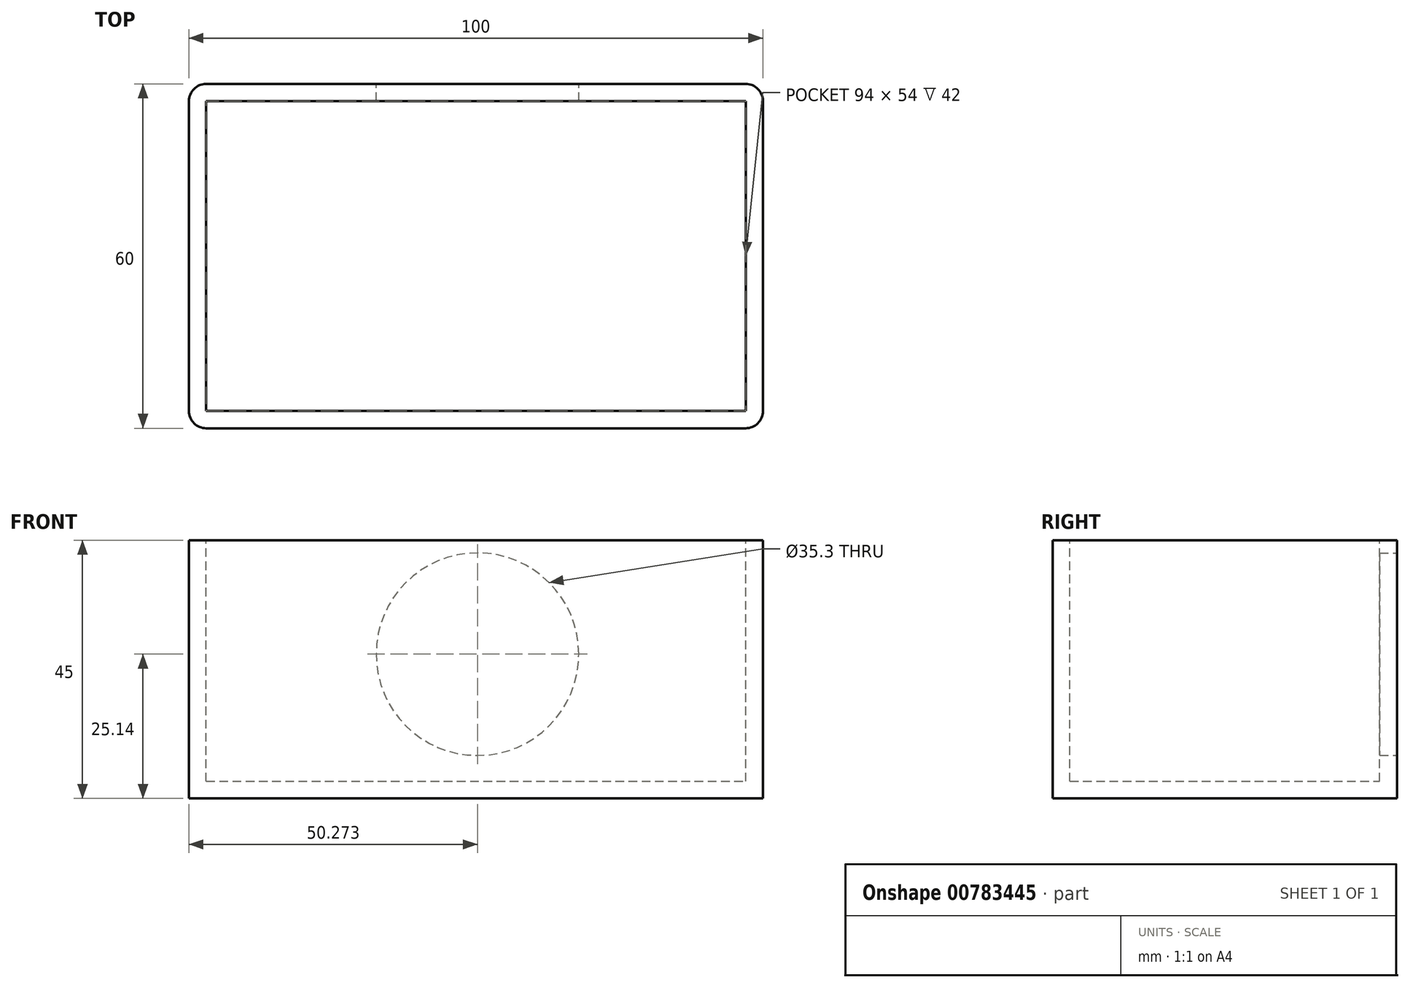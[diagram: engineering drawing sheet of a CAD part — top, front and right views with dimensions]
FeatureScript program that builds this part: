
annotation { "Feature Type Name" : "Feature", "Feature Type Description" : "" }
export const myFeature = defineFeature(function(context is Context, id is Id, definition is map)
    precondition{}
    {
        {
            var Q0;
            Q0=qCreatedBy(makeId("Top.planeOp"),FACE);
            var sketch = newSketch(context, id + "F0", { "sketchPlane" : qUnion([Q0])});
            skLineSegment(sketch, "E0", {"start": v(100, 0) * mm, "end": v(0, 0) * mm});
            skLineSegment(sketch, "E1", {"start": v(0, 0) * mm, "end": v(0, -60) * mm});
            skLineSegment(sketch, "E2", {"start": v(0, -60) * mm, "end": v(100, -60) * mm});
            skLineSegment(sketch, "E3", {"start": v(100, -60) * mm, "end": v(100, 0) * mm});
            skSolve(sketch);
        }
        {
            var Q0;
            Q0 = qSketchRegion(id + "F0", true);
            extrude(context, id + "F1", {"entities" : qUnion([Q0]), "depth" : 45 * mm, "offsetDistance" : 25 * mm});
        }
        {
            var Q0;
            Q0=makeQuery(id+"F1.opExtrude","CAP_FACE",FACE,{"disambiguationData":[OSD([sQuery(id+"F0.wireOp",EDGE,"E0"),sQuery(id+"F0.wireOp",EDGE,"E1"),sQuery(id+"F0.wireOp",EDGE,"E2"),sQuery(id+"F0.wireOp",EDGE,"E3")])],"isStart":false});
            var sketch = newSketch(context, id + "F2", { "sketchPlane" : qUnion([Q0])});
            skLineSegment(sketch, "E4.bottom", {"start": v(97, -3) * mm, "end": v(3, -3) * mm});
            skLineSegment(sketch, "E4.top", {"start": v(97, -57) * mm, "end": v(3, -57) * mm});
            skLineSegment(sketch, "E4.left", {"start": v(97, -3) * mm, "end": v(97, -57) * mm});
            skLineSegment(sketch, "E4.right", {"start": v(3, -3) * mm, "end": v(3, -57) * mm});
            skSolve(sketch);
        }
        {
            var Q0;
            Q0=makeQuery(id+"F2.imprint","IMPRINT",FACE,{"disambiguationData":[TD([[makeQuery(id+"F2.imprint","IMPRINT",EDGE,{"derivedFrom":sQuery(id+"F2.wireOp",EDGE,"E4.bottom")}),1.0]])]});
            var Q1;
            Q1=makeQuery(id+"F1.opExtrude","CAP_FACE",FACE,{"disambiguationData":[OSD([sQuery(id+"F0.wireOp",EDGE,"E0"),sQuery(id+"F0.wireOp",EDGE,"E1"),sQuery(id+"F0.wireOp",EDGE,"E2"),sQuery(id+"F0.wireOp",EDGE,"E3")])],"isStart":true});
            extrude(context, id + "F3", {"entities" : qUnion([Q0]), "operationType" : NewBodyOperationType.REMOVE, "endBound" : BoundingType.UP_TO_SURFACE, "oppositeDirection" : true, "depth" : 37 * mm, "endBoundEntityFace" : qUnion([Q1]), "hasOffset" : true, "offsetDistance" : 3 * mm});
        }
        {
            var Q0;
            Q0=makeQuery(id+"F1.opExtrude","SWEPT_EDGE",EDGE,{"disambiguationData":[OSD([sQuery(id+"F0.wireOp",EDGE,"E2"),sQuery(id+"F0.wireOp",EDGE,"E3")])]});
            var Q1;
            Q1=makeQuery(id+"F1.opExtrude","SWEPT_EDGE",EDGE,{"disambiguationData":[OSD([sQuery(id+"F0.wireOp",EDGE,"E0"),sQuery(id+"F0.wireOp",EDGE,"E3")])]});
            var Q2;
            Q2=makeQuery(id+"F1.opExtrude","SWEPT_EDGE",EDGE,{"disambiguationData":[OSD([sQuery(id+"F0.wireOp",EDGE,"E0"),sQuery(id+"F0.wireOp",EDGE,"E1")])]});
            var Q3;
            Q3=makeQuery(id+"F1.opExtrude","SWEPT_EDGE",EDGE,{"disambiguationData":[OSD([sQuery(id+"F0.wireOp",EDGE,"E1"),sQuery(id+"F0.wireOp",EDGE,"E2")])]});
            fillet(context, id + "F4", {"entities" : qUnion([Q0, Q1, Q2, Q3]), "radius" : 3 * mm, "tangentPropagation" : true, "allowEdgeOverflow" : false});
        }
        {
            var Q0;
            Q0=makeQuery(id+"F1.opExtrude","SWEPT_FACE",FACE,{"disambiguationData":[OSD([sQuery(id+"F0.wireOp",EDGE,"E0")])]});
            var sketch = newSketch(context, id + "F5", { "sketchPlane" : qUnion([Q0])});
            skCircle(sketch, "E5", {"center": v(-50.27, 25.14) * mm, "radius": 17.65 * mm});
            skSolve(sketch);
        }
        {
            var Q0;
            Q0=makeQuery(id+"F5.imprint","IMPRINT",FACE,{"disambiguationData":[TD([[makeQuery(id+"F5.imprint","IMPRINT",EDGE,{"derivedFrom":sQuery(id+"F5.wireOp",EDGE,"E5")}),1.0]])]});
            extrude(context, id + "F6", {"entities" : qUnion([Q0]), "operationType" : NewBodyOperationType.REMOVE, "oppositeDirection" : true, "depth" : 25 * mm, "offsetDistance" : 25 * mm});
        }
    });
